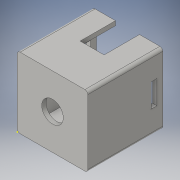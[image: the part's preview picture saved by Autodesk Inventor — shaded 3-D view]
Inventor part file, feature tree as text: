
AUTODESK INVENTOR PART (.ipt)
format: ipt  version: 2016 (Build 200138000, 138)  size: 165,376 bytes
history: native  units: in
note: dims shown in document units (in); Inventor stores cm internally (conversion verified against a paired STEP export)
features: sketch x6, extrude x5, fillet x1
ambient origin geometry x8: Origin, YZ Plane, XZ Plane, XY Plane, X Axis, Y Axis, Z Axis, Center Point
bodies: Solid1 (feature_tree)
feature tree (12):
  extrude  "Extrusion1"  Depth=3.0in
  sketch  "Sketch2"  dims[d2=0.185in d3=0.0in d5=0.915in]
  extrude  "Extrusion2"  Depth=0.185in
  extrude  "Extrusion4"  Depth=1.5in
  extrude  "Extrusion5"  Depth=0.185in
  extrude  "Extrusion6"  Depth=0.185in
  fillet  "Fillet2"  Radius=0.185in
  sketch  "Sketch1"  dims[d0=3.0in d1=3.0in]
  sketch  "Sketch3"  dims[d6=1.5in d7=1.5in]
  sketch  "Sketch5"  dims[d8=0.185in d9=0.0in d18=0.185in]
  sketch  "Sketch6"  dims[d19=0.185in d20=0.185in d21=0.185in]
  sketch  "Sketch7"  dims[d22=3.0in d23=0.0in d24=1.02in d25=1.502in d26=0.99in d27=0.99in d28=2.5in d29=0.0in d30=0.25in d31=1.0in d32=0.25in d33=1.0in d34=1.0in d35=2.5in d36=0.0in d37=0.125in]
